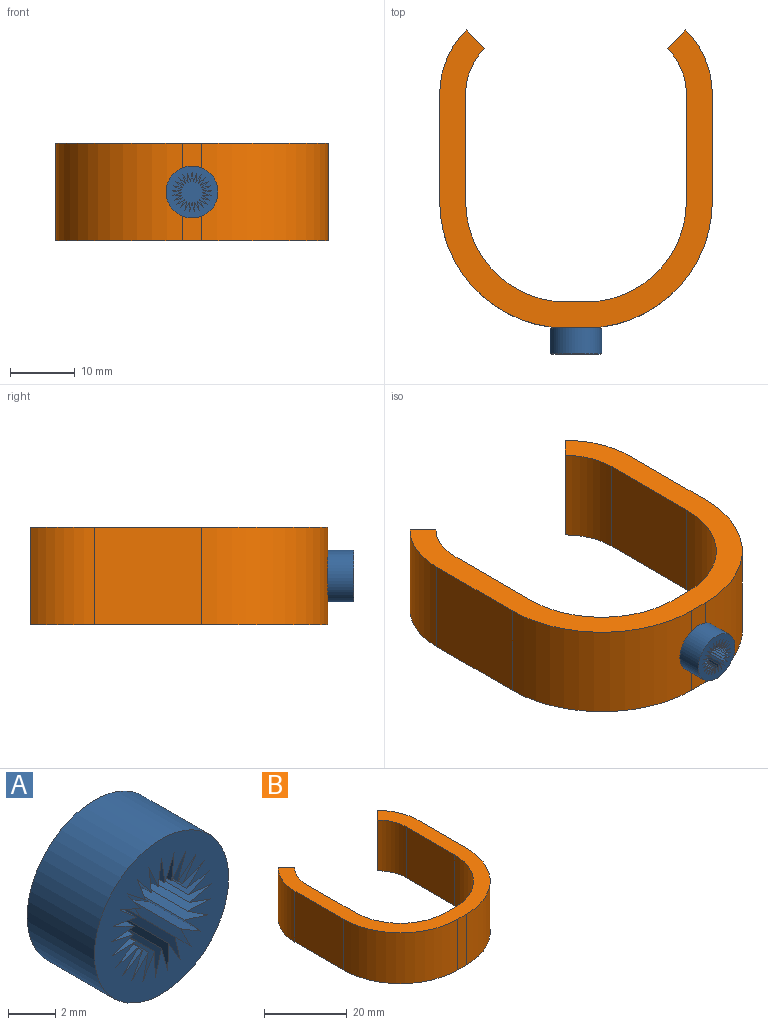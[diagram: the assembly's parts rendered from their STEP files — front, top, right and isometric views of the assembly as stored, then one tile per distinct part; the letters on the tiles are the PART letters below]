
ASSEMBLY  parts=2 mates=1
PART A: 54 faces, bbox 8x4x8 mm
  f0: plane 3x1.14mm, normal (0.82,0,0.57), area 4.1mm2, adj f1,f49,f51,f53
  f1: plane 3x1.08mm, normal (-0.62,0,-0.79), area 4.1mm2, adj f0,f2,f51,f53
  f2: plane 3x1.29mm, normal (0.94,0,0.34), area 4.1mm2, adj f1,f3,f51,f53
  f3: plane 3x1.09mm, normal (-0.79,0,-0.61), area 4.1mm2, adj f2,f4,f51,f53
  f4: plane 3x1.37mm, normal (0.99,0,0.1), area 4.1mm2, adj f3,f5,f51,f53
  f5: plane 3x1.27mm, normal (-0.92,0,-0.39), area 4.1mm2, adj f4,f6,f51,f53
  f6: plane 3x1.36mm, normal (0.99,0,-0.15), area 4.1mm2, adj f5,f7,f51,f53
  f7: plane 3x1.36mm, normal (-0.99,0,-0.15), area 4.1mm2, adj f6,f8,f51,f53
  f8: plane 3x1.27mm, normal (0.92,0,-0.39), area 4.1mm2, adj f7,f9,f51,f53
  f9: plane 3x1.37mm, normal (-0.99,0,0.1), area 4.1mm2, adj f8,f10,f51,f53
  f10: plane 3x1.09mm, normal (0.79,0,-0.61), area 4.1mm2, adj f9,f11,f51,f53
  f11: plane 3x1.29mm, normal (-0.94,0,0.34), area 4.1mm2, adj f10,f12,f51,f53
  f12: plane 3x1.08mm, normal (0.62,0,-0.79), area 4.1mm2, adj f11,f13,f51,f53
  f13: plane 3x1.14mm, normal (-0.82,0,0.57), area 4.1mm2, adj f12,f14,f51,f53
  f14: plane 3x1.26mm, normal (0.4,0,-0.92), area 4.1mm2, adj f13,f15,f51,f53
  f15: plane 3x1.04mm, normal (-0.66,0,0.75), area 4.1mm2, adj f14,f16,f51,f53
  f16: plane 3x1.36mm, normal (0.16,0,-0.99), area 4.1mm2, adj f15,f17,f51,f53
  f17: plane 3x1.23mm, normal (-0.45,0,0.89), area 4.1mm2, adj f16,f18,f51,f53
  f18: plane 3x1.37mm, normal (-0.09,0,-1), area 4.1mm2, adj f17,f19,f51,f53
  f19: plane 3x1.35mm, normal (-0.21,0,0.98), area 4.1mm2, adj f18,f20,f51,f53
  f20: plane 3x1.3mm, normal (-0.33,0,-0.94), area 4.1mm2, adj f19,f21,f51,f53
  f21: plane 3x1.38mm, normal (0.04,0,1), area 4.1mm2, adj f20,f22,f51,f53
  f22: plane 3x1.15mm, normal (-0.56,0,-0.83), area 4.1mm2, adj f21,f23,f51,f53
  f23: plane 3x1.32mm, normal (0.29,0,0.96), area 4.1mm2, adj f22,f24,f51,f53
  f24: plane 3x1.03mm, normal (-0.75,0,-0.67), area 4.1mm2, adj f23,f25,f51,f53
  f25: plane 3x1.18mm, normal (0.51,0,0.86), area 4.1mm2, adj f24,f26,f51,f53
  f26: plane 3x1.22mm, normal (-0.89,0,-0.46), area 4.1mm2, adj f25,f27,f51,f53
  f27: plane 3x0.98mm, normal (0.71,0,0.7), area 4.1mm2, adj f26,f28,f51,f53
  f28: plane 3x1.34mm, normal (-0.97,0,-0.22), area 4.1mm2, adj f27,f29,f51,f53
  f29: plane 3x1.19mm, normal (0.86,0,0.5), area 4.1mm2, adj f28,f30,f51,f53
  f30: plane 3x1.38mm, normal (-1,0,0.02), area 4.1mm2, adj f29,f31,f51,f53
  f31: plane 3x1.33mm, normal (0.96,0,0.27), area 4.1mm2, adj f30,f32,f51,f53
  f32: plane 3x1.33mm, normal (-0.96,0,0.27), area 4.1mm2, adj f31,f33,f51,f53
  f33: plane 3x1.38mm, normal (1,0,0.02), area 4.1mm2, adj f32,f34,f51,f53
  f34: plane 3x1.19mm, normal (-0.86,0,0.5), area 4.1mm2, adj f33,f35,f51,f53
  f35: plane 3x1.34mm, normal (0.97,0,-0.22), area 4.1mm2, adj f34,f36,f51,f53
  f36: plane 3x0.98mm, normal (-0.71,0,0.7), area 4.1mm2, adj f35,f37,f51,f53
  f37: plane 3x1.22mm, normal (0.89,0,-0.46), area 4.1mm2, adj f36,f38,f51,f53
  f38: plane 3x1.18mm, normal (-0.51,0,0.86), area 4.1mm2, adj f37,f39,f51,f53
  f39: plane 3x1.03mm, normal (0.75,0,-0.67), area 4.1mm2, adj f38,f40,f51,f53
  f40: plane 3x1.32mm, normal (-0.29,0,0.96), area 4.1mm2, adj f39,f41,f51,f53
  f41: plane 3x1.15mm, normal (0.56,0,-0.83), area 4.1mm2, adj f40,f42,f51,f53
  f42: plane 3x1.38mm, normal (-0.04,0,1), area 4.1mm2, adj f41,f43,f51,f53
  f43: plane 3x1.3mm, normal (0.33,0,-0.94), area 4.1mm2, adj f42,f44,f51,f53
  f44: plane 3x1.35mm, normal (0.21,0,0.98), area 4.1mm2, adj f43,f45,f51,f53
  f45: plane 3x1.37mm, normal (0.09,0,-1), area 4.1mm2, adj f44,f46,f51,f53
  f46: plane 3x1.23mm, normal (0.45,0,0.89), area 4.1mm2, adj f45,f47,f51,f53
  f47: plane 3x1.36mm, normal (-0.16,0,-0.99), area 4.1mm2, adj f46,f48,f51,f53
  f48: plane 3x1.04mm, normal (0.66,0,0.75), area 4.1mm2, adj f47,f49,f51,f53
  f49: plane 3x1.26mm, normal (-0.4,0,-0.92), area 4.1mm2, adj f0,f48,f51,f53
  f50: cylinder r=4mm len=8mm, axis (0,1,0), area 100.5mm2, adj f51,f52
  f51: plane 8x8mm, normal (0,-1,0), area 34.8mm2, adj f0,f1,f2,f3,f4,f5,f6,f7
  f52: plane 8x8mm, normal (0,1,0), area 50.3mm2, adj f50
  f53: plane 5.99x5.98mm, normal (0,-1,0), area 15.5mm2, adj f0,f1,f2,f3,f4,f5,f6,f7
PART B: 18 faces, bbox 42x45.9x15 mm
  f0: cylinder r=10mm len=15mm, axis (0,0,-1), area 117.8mm2, adj f1,f15,f16,f17
  f1: plane 16.5x15mm, normal (-1,0,0), area 247.5mm2, adj f0,f2,f16,f17
  f2: cylinder r=15.5mm len=15.5mm, axis (0,0,-1), area 365.2mm2, adj f1,f3,f16,f17
  f3: plane 15x3mm, normal (0,1,0), area 45mm2, adj f2,f4,f16,f17
  f4: cylinder r=15.5mm len=15.5mm, axis (0,0,-1), area 365.2mm2, adj f3,f5,f16,f17
  f5: plane 16.5x15mm, normal (1,0,0), area 247.5mm2, adj f4,f6,f16,f17
  f6: cylinder r=10mm len=15mm, axis (0,0,-1), area 117.8mm2, adj f5,f7,f16,f17
  f7: plane 15x2.83mm, normal (0.71,0.71,0), area 60mm2, adj f6,f8,f16,f17
  f8: cylinder r=14mm len=15mm, axis (0,0,-1), area 164.9mm2, adj f7,f9,f16,f17
  f9: plane 16.5x15mm, normal (-1,0,0), area 247.5mm2, adj f8,f10,f16,f17
  f10: cylinder r=19.5mm len=19.5mm, axis (0,0,-1), area 459.5mm2, adj f9,f11,f16,f17
  f11: plane 15x3mm, normal (0,-1,0), area 45mm2, adj f10,f12,f16,f17
  f12: cylinder r=19.5mm len=19.5mm, axis (0,0,-1), area 459.5mm2, adj f11,f13,f16,f17
  f13: plane 16.5x15mm, normal (1,0,0), area 247.5mm2, adj f12,f14,f16,f17
  f14: cylinder r=14mm len=15mm, axis (0,0,-1), area 164.9mm2, adj f13,f15,f16,f17
  f15: plane 15x2.83mm, normal (-0.71,0.71,0), area 60mm2, adj f0,f14,f16,f17
  f16: plane 45.9x42mm, normal (0,0,1), area 439.3mm2, adj f0,f1,f2,f3,f4,f5,f6,f7
  f17: plane 45.9x42mm, normal (0,0,-1), area 439.3mm2, adj f0,f1,f2,f3,f4,f5,f6,f7
PLACE A t=(-2.95,3.99,-2.95)mm
PLACE B t=(-2.95,29.99,-10.45)mm
MATE fastened B.f11 <-> A.f50  axis (0,-1,0) through (-2.95,4.99,-2.95)mm
